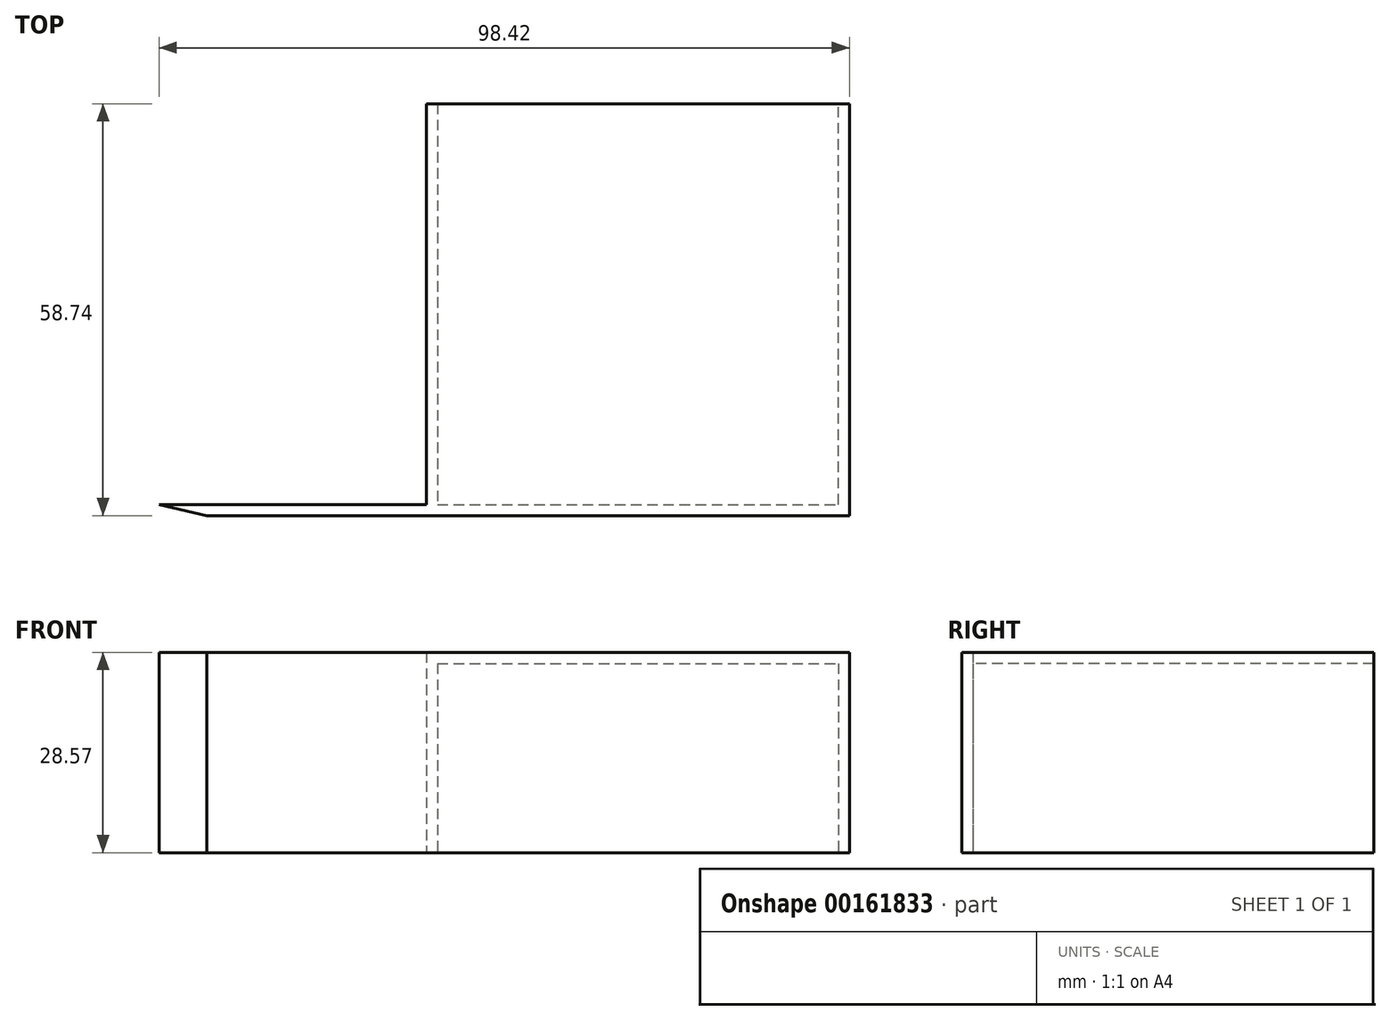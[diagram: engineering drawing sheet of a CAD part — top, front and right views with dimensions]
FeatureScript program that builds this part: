
annotation { "Feature Type Name" : "Feature", "Feature Type Description" : "" }
export const myFeature = defineFeature(function(context is Context, id is Id, definition is map)
    precondition{}
    {
        {
            var Q0;
            Q0=qCreatedBy(makeId("Top.planeOp"),FACE);
            var sketch = newSketch(context, id + "F0", { "sketchPlane" : qUnion([Q0])});
            skLineSegment(sketch, "E0", {"start": v(0, 0) * mm, "end": v(38.1, 0) * mm});
            skLineSegment(sketch, "E1", {"start": v(38.1, 0) * mm, "end": v(38.1, 57.15) * mm});
            skLineSegment(sketch, "E2", {"start": v(38.1, 57.15) * mm, "end": v(39.69, 57.15) * mm});
            skLineSegment(sketch, "E3", {"start": v(6.82, -1.59) * mm, "end": v(98.42, -1.59) * mm});
            skLineSegment(sketch, "E4", {"start": v(98.42, -1.59) * mm, "end": v(98.42, 57.15) * mm});
            skLineSegment(sketch, "E5", {"start": v(98.43, 57.15) * mm, "end": v(96.84, 57.15) * mm});
            skLineSegment(sketch, "E6", {"start": v(39.69, 57.15) * mm, "end": v(39.69, 0) * mm});
            skLineSegment(sketch, "E7", {"start": v(39.69, 0) * mm, "end": v(96.84, 0) * mm});
            skLineSegment(sketch, "E8", {"start": v(96.84, 0) * mm, "end": v(96.84, 57.15) * mm});
            skLineSegment(sketch, "E9", {"start": v(0, 0) * mm, "end": v(6.82, -1.59) * mm});
            skSolve(sketch);
        }
        {
            var Q0;
            Q0=qSketchRegion(id+"F0",true);
            extrude(context, id + "F1", {"entities" : qUnion([Q0]), "depth" : 28.57 * mm});
        }
        {
            var Q0;
            Q0=makeQuery(id+"F1.opExtrude","CAP_FACE",FACE,{"disambiguationData":[OSD([sQuery(id+"F0.wireOp",EDGE,"E0"),sQuery(id+"F0.wireOp",EDGE,"E1"),sQuery(id+"F0.wireOp",EDGE,"E2"),sQuery(id+"F0.wireOp",EDGE,"E3"),sQuery(id+"F0.wireOp",EDGE,"E4"),sQuery(id+"F0.wireOp",EDGE,"E5"),sQuery(id+"F0.wireOp",EDGE,"E6"),sQuery(id+"F0.wireOp",EDGE,"E7"),sQuery(id+"F0.wireOp",EDGE,"E8"),sQuery(id+"F0.wireOp",EDGE,"E9")])],"isStart":false});
            var sketch = newSketch(context, id + "F2", { "sketchPlane" : qUnion([Q0])});
            skLineSegment(sketch, "E10.bottom", {"start": v(39.69, 0) * mm, "end": v(96.84, 0) * mm});
            skLineSegment(sketch, "E10.top", {"start": v(39.69, 57.15) * mm, "end": v(96.84, 57.15) * mm});
            skLineSegment(sketch, "E10.left", {"start": v(39.69, 0) * mm, "end": v(39.69, 57.15) * mm});
            skLineSegment(sketch, "E10.right", {"start": v(96.84, 0) * mm, "end": v(96.84, 57.15) * mm});
            skSolve(sketch);
        }
        {
            var Q0;
            Q0 = qSketchRegion(id + "F2", true);
            extrude(context, id + "F3", {"entities" : qUnion([Q0]), "operationType" : NewBodyOperationType.ADD, "oppositeDirection" : true, "depth" : 1.59 * mm});
        }
    });
